# Revit family: Gira_531900
name_source: partatom
category: Electrical Fixtures
revit_build: Autodesk Revit 2017 (Build: 20160225_1515(x64)
units: mm (PartAtom-declared; Revit-internal decimal feet)

## family parameters
Cut with Voids When Loaded = No
Host = Face
Maintain Annotation Orientation = No
Part Type = Normal
Room Calculation Point = No
Round Connector Dimension = Use Diameter
Shared = No

## types (1)
- Pow.supply DC 12 V 2  A DRA Accessories
    BIM = https://media.live.bim.site 2f.rfa
    BIMSITE_PRODUCT_ID = d6225ded82d3066a22a992929dfc11803a763672
    Cost = 0 $
    Default Elevation = 1219 mm
    Description = PS DC 12V 2A DRA Zub. Power supply DC 12 V   2 A ,DRA Features: - Power supply DC 12 V for the eNet server, eNet radio reception module and external camera.
    GTIN = 4010337774037
    HAN = 531900
    HeinzeBIM = https://www.heinze.de
    Manufacturer = Gira
    URL = https://www.gira.de

## geometry (parser evidence)
native form markers: Blend x2, Sweep x3
no freeform markers — native parametric forms only
